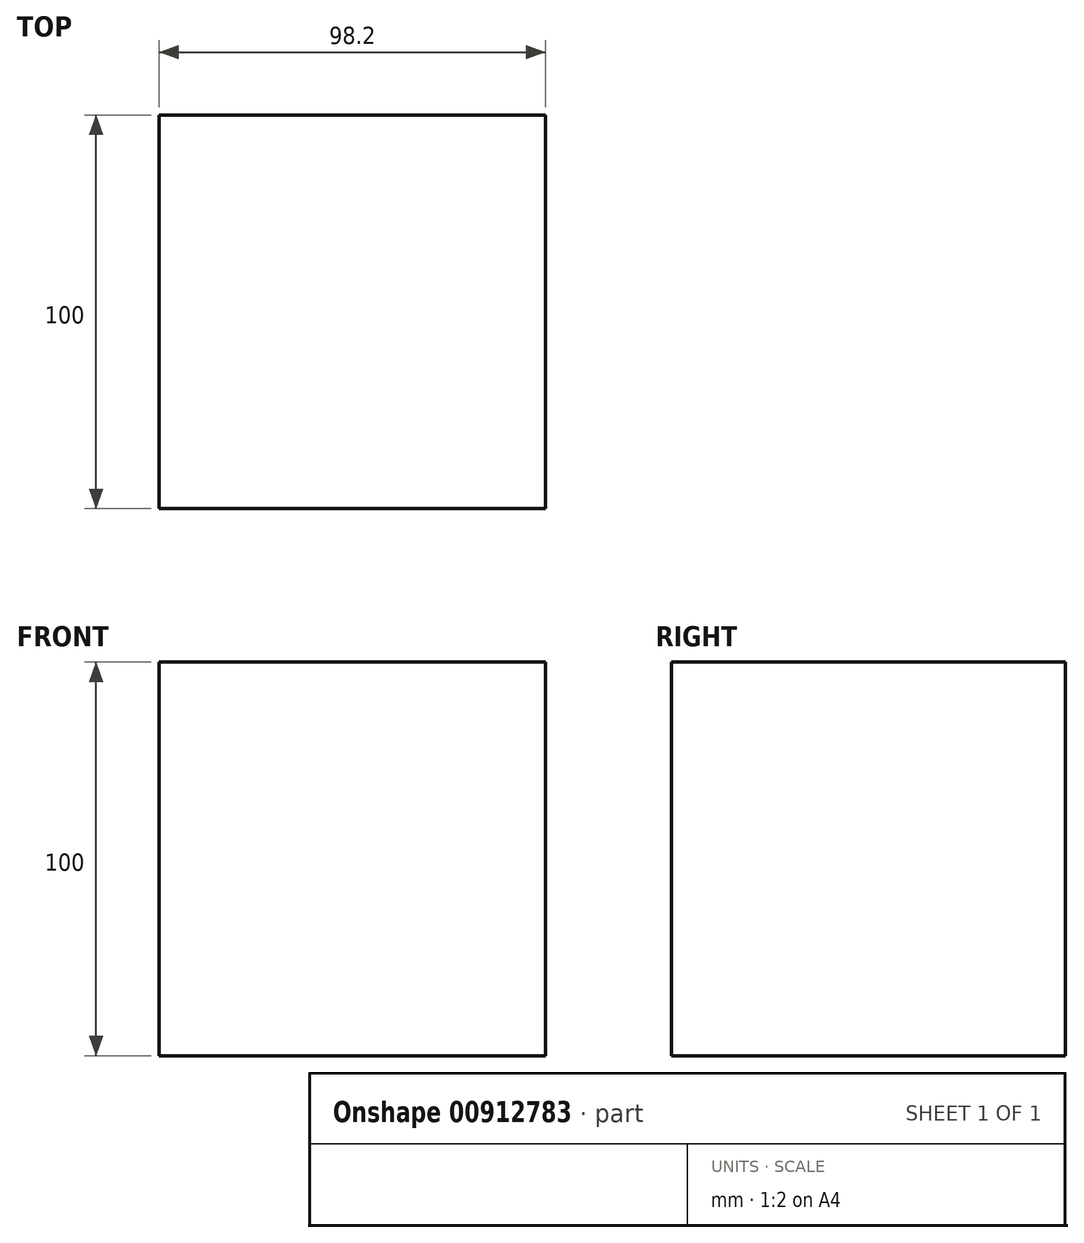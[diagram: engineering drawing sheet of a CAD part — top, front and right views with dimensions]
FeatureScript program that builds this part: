
annotation { "Feature Type Name" : "Feature", "Feature Type Description" : "" }
export const myFeature = defineFeature(function(context is Context, id is Id, definition is map)
    precondition{}
    {
        {
            var Q0;
            Q0=qCreatedBy(makeId("Top.planeOp"),FACE);
            var sketch = newSketch(context, id + "F0", { "sketchPlane" : qUnion([Q0])});
            skLineSegment(sketch, "E0.bottom", {"start": v(49.1, -50) * mm, "end": v(-49.1, -50) * mm});
            skLineSegment(sketch, "E0.top", {"start": v(49.1, 50) * mm, "end": v(-49.1, 50) * mm});
            skLineSegment(sketch, "E0.left", {"start": v(49.1, -50) * mm, "end": v(49.1, 50) * mm});
            skLineSegment(sketch, "E0.right", {"start": v(-49.1, -50) * mm, "end": v(-49.1, 50) * mm});
            skPoint(sketch, "E0.middle", {"position": v(0, 0) * mm});
            skSolve(sketch);
        }
        {
            var Q0;
            Q0 = qSketchRegion(id + "F0", true);
            extrude(context, id + "F1", {"entities" : qUnion([Q0]), "depth" : 100 * mm, "offsetDistance" : 25 * mm});
        }
    });
